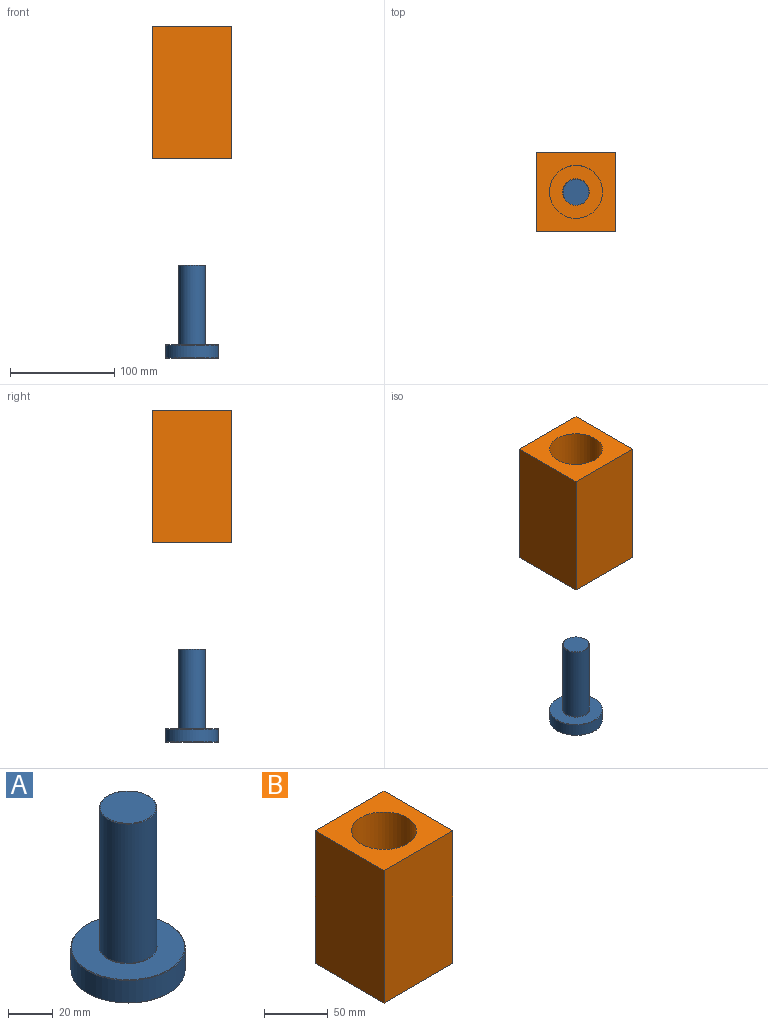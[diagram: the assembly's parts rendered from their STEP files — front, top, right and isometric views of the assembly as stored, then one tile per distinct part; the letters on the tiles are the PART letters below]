
ASSEMBLY  parts=2 mates=1
PART A: 9 faces, bbox 50.8x50.8x88.9 mm
  f0: cylinder r=25.4mm len=50.8mm, axis (0,0,-1), area 1947mm2, adj f5,f6
  f1: plane 50.3x50.3mm, normal (0,0,1), area 1464.3mm2, adj f6,f8
  f2: plane 50.3x50.3mm, normal (0,0,-1), area 1987.1mm2, adj f5
  f3: cylinder r=12.7mm len=75.75mm, axis (0,0,-1), area 6044.6mm2, adj f7,f8
  f4: plane 24.9x24.9mm, normal (0,0,1), area 487mm2, adj f7
  f5: cone r=25.4mm half-angle=45deg, axis (0,0,1), area 56.1mm2, adj f0,f2
  f6: cone r=25.15mm half-angle=45deg, axis (0,0,-1), area 56.1mm2, adj f0,f1
  f7: cone r=12.45mm half-angle=45deg, axis (0,0,-1), area 27.9mm2, adj f3,f4
  f8: torus R=12.9mm, axis (0,0,1), area 25.2mm2, adj f1,f3
PART B: 9 faces, bbox 76.2x76.2x127 mm
  f0: plane 127x76.2mm, normal (-1,0,0), area 9677.4mm2, adj f1,f3,f4,f5
  f1: plane 127x76.2mm, normal (0,-1,0), area 9677.4mm2, adj f0,f2,f4,f5
  f2: plane 127x76.2mm, normal (1,0,0), area 9677.4mm2, adj f1,f3,f4,f5
  f3: plane 127x76.2mm, normal (0,1,0), area 9677.4mm2, adj f0,f2,f4,f5
  f4: plane 76.2x76.2mm, normal (0,0,1), area 3779.6mm2, adj f0,f1,f2,f3,f6
  f5: plane 76.2x76.2mm, normal (0,0,-1), area 5299.7mm2, adj f0,f1,f2,f3,f8
  f6: cylinder r=25.4mm len=63.5mm, axis (0,0,1), area 10134.1mm2, adj f4,f7
  f7: plane 50.8x50.8mm, normal (0,0,1), area 1520.1mm2, adj f6,f8
  f8: cylinder r=12.7mm len=63.5mm, axis (0,0,1), area 5067.1mm2, adj f5,f7
PLACE A rot(axis=(0,0,-1),57.8deg) t=(38.1,38.1,-191.03)mm
PLACE B at identity fixed
MATE cylindrical A.f3 <-> B.f6  axis (0,0,-1) through (38.1,38.1,-140.26)mm
